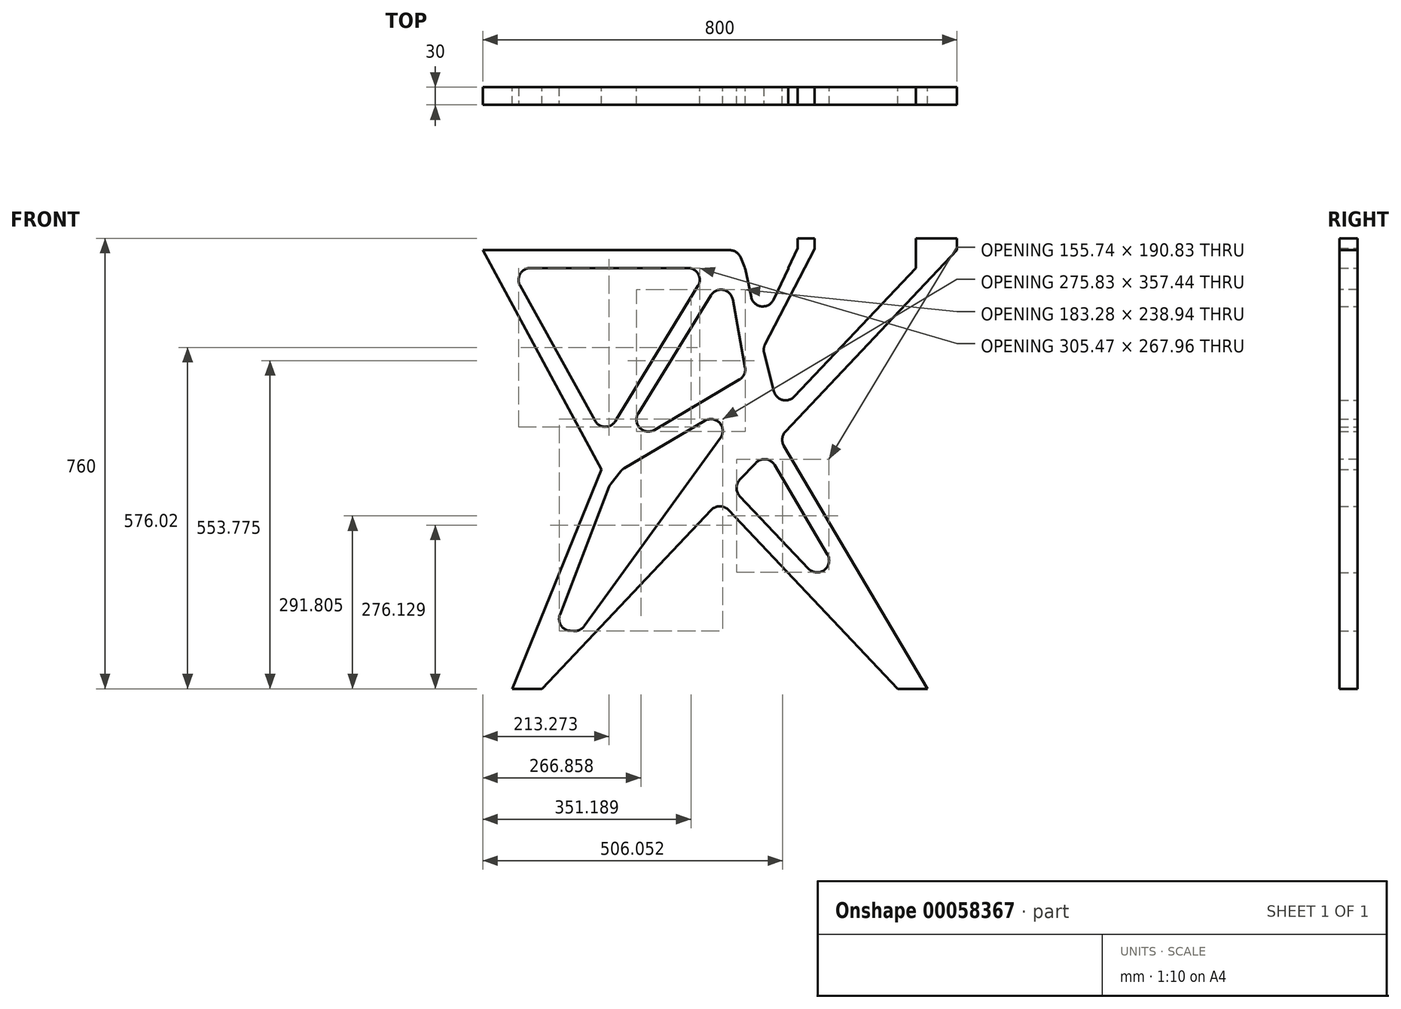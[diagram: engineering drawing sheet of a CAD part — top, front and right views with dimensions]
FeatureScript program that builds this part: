
annotation { "Feature Type Name" : "Feature", "Feature Type Description" : "" }
export const myFeature = defineFeature(function(context is Context, id is Id, definition is map)
    precondition{}
    {
        {
            var Q0;
            Q0=qCreatedBy(makeId("Front.planeOp"),FACE);
            var sketch = newSketch(context, id + "F0", { "sketchPlane" : qUnion([Q0])});
            skLineSegment(sketch, "E0", {"start": v(-40.37, 370) * mm, "end": v(-40.37, -370) * mm, "construction": true});
            skLineSegment(sketch, "E1", {"start": v(-40.37, 370) * mm, "end": v(759.63, 370) * mm, "construction": true});
            skLineSegment(sketch, "E2", {"start": v(-40.37, 370) * mm, "end": v(359.63, 370) * mm, "construction": true});
            skLineSegment(sketch, "E3", {"start": v(-40.37, -370) * mm, "end": v(759.63, -370) * mm, "construction": true});
            skLineSegment(sketch, "E4", {"start": v(759.63, -370) * mm, "end": v(359.63, -370) * mm, "construction": true});
            skLineSegment(sketch, "E5", {"start": v(-40.37, -370) * mm, "end": v(-40.37, 0) * mm, "construction": true});
            skLineSegment(sketch, "E6", {"start": v(-40.37, -370) * mm, "end": v(359.63, -370) * mm, "construction": true});
            skLineSegment(sketch, "E7", {"start": v(159.63, -370) * mm, "end": v(-40.37, -370) * mm, "construction": true});
            skLineSegment(sketch, "E8", {"start": v(59.63, -370) * mm, "end": v(759.63, 370) * mm, "construction": true});
            skLineSegment(sketch, "E9", {"start": v(59.63, -370) * mm, "end": v(-40.37, -370) * mm, "construction": true});
            skLineSegment(sketch, "E10", {"start": v(159.63, 0) * mm, "end": v(9.63, -370) * mm, "construction": true});
            skLineSegment(sketch, "E11", {"start": v(9.63, -370) * mm, "end": v(59.63, -370) * mm});
            skLineSegment(sketch, "E12", {"start": v(759.63, 370) * mm, "end": v(59.63, -370) * mm});
            skLineSegment(sketch, "E13", {"start": v(9.63, -370) * mm, "end": v(159.63, 0) * mm});
            skLineSegment(sketch, "E14", {"start": v(-40.37, 370) * mm, "end": v(159.63, 0) * mm});
            skLineSegment(sketch, "E15", {"start": v(-40.37, 370) * mm, "end": v(-10.37, 370) * mm, "construction": true});
            skLineSegment(sketch, "E16", {"start": v(-10.37, 370) * mm, "end": v(165.48, 52.28) * mm, "construction": true});
            skLineSegment(sketch, "E17", {"start": v(-10.37, 370) * mm, "end": v(359.63, 370) * mm, "construction": true});
            skLineSegment(sketch, "E18", {"start": v(165.48, 52.28) * mm, "end": v(359.63, 370) * mm, "construction": true});
            skLineSegment(sketch, "E19", {"start": v(359.63, 370) * mm, "end": v(389.63, 370) * mm, "construction": true});
            skLineSegment(sketch, "E20", {"start": v(165.48, 52.28) * mm, "end": v(179.74, 25.89) * mm, "construction": true});
            skLineSegment(sketch, "E21", {"start": v(389.63, 370) * mm, "end": v(179.74, 25.89) * mm, "construction": true});
            skLineSegment(sketch, "E22", {"start": v(-40.37, -370) * mm, "end": v(-40.37, -270) * mm, "construction": true});
            skLineSegment(sketch, "E23", {"start": v(154.23, -270) * mm, "end": v(124.23, -273.43) * mm, "construction": true});
            skLineSegment(sketch, "E24", {"start": v(50.17, -270) * mm, "end": v(80.17, -282.16) * mm, "construction": true});
            skLineSegment(sketch, "E25", {"start": v(80.17, -270) * mm, "end": v(173.9, -26.4) * mm, "construction": true});
            skLineSegment(sketch, "E26", {"start": v(173.9, 370) * mm, "end": v(173.9, 340) * mm, "construction": true});
            skLineSegment(sketch, "E27", {"start": v(173.9, 340) * mm, "end": v(6.24, 340) * mm, "construction": true});
            skLineSegment(sketch, "E28", {"start": v(6.24, 340) * mm, "end": v(173.9, 340) * mm, "construction": true});
            skLineSegment(sketch, "E29", {"start": v(173.9, 340) * mm, "end": v(341.3, 340) * mm, "construction": true});
            skLineSegment(sketch, "E30", {"start": v(341.3, 340) * mm, "end": v(389.63, 370) * mm, "construction": true});
            skLineSegment(sketch, "E31", {"start": v(389.63, 370) * mm, "end": v(489.63, 370) * mm, "construction": true});
            skLineSegment(sketch, "E32", {"start": v(416.87, 131.07) * mm, "end": v(194.9, 0) * mm, "construction": true});
            skLineSegment(sketch, "E33", {"start": v(194.9, 0) * mm, "end": v(179.74, 25.89) * mm, "construction": true});
            skLineSegment(sketch, "E34", {"start": v(179.74, 25.89) * mm, "end": v(404.64, 158.69) * mm, "construction": true});
            skLineSegment(sketch, "E35", {"start": v(404.64, 158.69) * mm, "end": v(371.34, 340) * mm, "construction": true});
            skLineSegment(sketch, "E36", {"start": v(371.34, 340) * mm, "end": v(731.26, 340) * mm, "construction": true});
            skLineSegment(sketch, "E37", {"start": v(690.24, 340) * mm, "end": v(401.89, 340) * mm, "construction": true});
            skLineSegment(sketch, "E38", {"start": v(401.89, 340) * mm, "end": v(371.93, 338.33) * mm, "construction": true});
            skLineSegment(sketch, "E39", {"start": v(401.89, 340) * mm, "end": v(459.98, 96.59) * mm, "construction": true});
            skLineSegment(sketch, "E40", {"start": v(389.63, 370) * mm, "end": v(-40.37, 370) * mm});
            skLineSegment(sketch, "E41", {"start": v(359.63, 370) * mm, "end": v(389.63, 370) * mm});
            skLineSegment(sketch, "E42", {"start": v(690.24, 340) * mm, "end": v(459.98, 96.59) * mm});
            skLineSegment(sketch, "E43", {"start": v(690.24, 340) * mm, "end": v(690.24, 370) * mm});
            skLineSegment(sketch, "E44", {"start": v(6.24, 340) * mm, "end": v(341.3, 340) * mm});
            skLineSegment(sketch, "E45", {"start": v(165.48, 52.28) * mm, "end": v(341.3, 340) * mm});
            skLineSegment(sketch, "E46", {"start": v(165.48, 52.28) * mm, "end": v(6.24, 340) * mm});
            skLineSegment(sketch, "E47", {"start": v(371.93, 338.33) * mm, "end": v(404.64, 158.69) * mm});
            skLineSegment(sketch, "E48", {"start": v(179.74, 25.89) * mm, "end": v(371.93, 338.33) * mm});
            skLineSegment(sketch, "E49", {"start": v(401.89, 340) * mm, "end": v(690.24, 340) * mm});
            skLineSegment(sketch, "E50", {"start": v(179.74, 25.89) * mm, "end": v(404.64, 158.69) * mm});
            skLineSegment(sketch, "E51", {"start": v(489.63, 370) * mm, "end": v(424.8, 233.3) * mm, "construction": true});
            skLineSegment(sketch, "E52", {"start": v(490.63, 373.24) * mm, "end": v(519.58, 371.85) * mm, "construction": true});
            skLineSegment(sketch, "E53", {"start": v(424.8, 233.3) * mm, "end": v(432.28, 204.24) * mm, "construction": true});
            skLineSegment(sketch, "E54", {"start": v(690.24, 370) * mm, "end": v(759.63, 370) * mm});
            skLineSegment(sketch, "E55", {"start": v(519.58, 371.85) * mm, "end": v(490.63, 373.24) * mm});
            skLineSegment(sketch, "E56", {"start": v(389.63, 370) * mm, "end": v(359.63, 370) * mm});
            skLineSegment(sketch, "E57", {"start": v(341.3, 340) * mm, "end": v(6.24, 340) * mm});
            skLineSegment(sketch, "E58", {"start": v(-10.37, 370) * mm, "end": v(-40.37, 370) * mm});
            skLineSegment(sketch, "E59", {"start": v(490.63, 373.24) * mm, "end": v(519.58, 371.85) * mm});
            skLineSegment(sketch, "E60", {"start": v(416.87, 131.07) * mm, "end": v(124.23, -273.43) * mm, "construction": true});
            skLineSegment(sketch, "E61", {"start": v(194.9, 0) * mm, "end": v(173.9, -26.4) * mm});
            skLineSegment(sketch, "E62", {"start": v(173.9, -26.4) * mm, "end": v(80.17, -270) * mm});
            skLineSegment(sketch, "E63", {"start": v(80.17, -270) * mm, "end": v(124.23, -273.43) * mm});
            skLineSegment(sketch, "E64", {"start": v(416.87, 131.07) * mm, "end": v(124.23, -273.43) * mm});
            skLineSegment(sketch, "E65", {"start": v(416.87, 131.07) * mm, "end": v(194.9, 0) * mm});
            skLineSegment(sketch, "E66", {"start": v(424.8, 233.3) * mm, "end": v(489.63, 370) * mm});
            skLineSegment(sketch, "E67", {"start": v(519.58, 371.85) * mm, "end": v(432.28, 204.24) * mm});
            skLineSegment(sketch, "E68", {"start": v(389.63, 370) * mm, "end": v(401.89, 340) * mm});
            skLineSegment(sketch, "E69", {"start": v(424.8, 233.3) * mm, "end": v(401.89, 340) * mm});
            skLineSegment(sketch, "E70", {"start": v(432.28, 204.24) * mm, "end": v(459.98, 96.59) * mm});
            skLineSegment(sketch, "E71", {"start": v(-40.37, 370) * mm, "end": v(-40.37, 390) * mm});
            skLineSegment(sketch, "E72", {"start": v(-40.37, 390) * mm, "end": v(-10.37, 390) * mm});
            skLineSegment(sketch, "E73", {"start": v(-10.37, 390) * mm, "end": v(-10.37, 370) * mm});
            skLineSegment(sketch, "E74", {"start": v(359.63, 370) * mm, "end": v(359.63, 390) * mm});
            skLineSegment(sketch, "E75", {"start": v(359.63, 390) * mm, "end": v(389.63, 390) * mm});
            skLineSegment(sketch, "E76", {"start": v(389.63, 390) * mm, "end": v(389.63, 370) * mm});
            skLineSegment(sketch, "E77", {"start": v(490.63, 373.24) * mm, "end": v(490.63, 390) * mm});
            skLineSegment(sketch, "E78", {"start": v(490.63, 390) * mm, "end": v(519.58, 390) * mm});
            skLineSegment(sketch, "E79", {"start": v(519.58, 390) * mm, "end": v(519.58, 371.85) * mm});
            skLineSegment(sketch, "E80", {"start": v(690.24, 370) * mm, "end": v(690.24, 390) * mm});
            skLineSegment(sketch, "E81", {"start": v(690.24, 390) * mm, "end": v(759.63, 390) * mm});
            skLineSegment(sketch, "E82", {"start": v(759.63, 390) * mm, "end": v(759.63, 370) * mm});
            skLineSegment(sketch, "E83", {"start": v(490.63, 373.24) * mm, "end": v(424.8, 233.3) * mm});
            skLineSegment(sketch, "E84", {"start": v(59.63, -370) * mm, "end": v(533.62, 131.07) * mm, "construction": true});
            skLineSegment(sketch, "E85", {"start": v(533.62, 131.07) * mm, "end": v(287.67, -128.93) * mm, "construction": true});
            skLineSegment(sketch, "E86", {"start": v(759.63, -370) * mm, "end": v(709.63, -370) * mm, "construction": true});
            skLineSegment(sketch, "E87", {"start": v(287.67, -128.93) * mm, "end": v(287.67, -370) * mm, "construction": true});
            skLineSegment(sketch, "E88", {"start": v(287.67, -370) * mm, "end": v(515.71, -370) * mm, "construction": true});
            skLineSegment(sketch, "E89", {"start": v(359.63, 390) * mm, "end": v(359.63, -370) * mm, "construction": true});
            skLineSegment(sketch, "E90", {"start": v(359.63, -370) * mm, "end": v(709.63, -370) * mm, "construction": true});
            skLineSegment(sketch, "E91", {"start": v(359.63, -370) * mm, "end": v(659.63, -370) * mm, "construction": true});
            skLineSegment(sketch, "E92", {"start": v(359.63, -52.86) * mm, "end": v(659.63, -370) * mm});
            skLineSegment(sketch, "E93", {"start": v(659.63, -370) * mm, "end": v(709.63, -370) * mm});
            skLineSegment(sketch, "E94", {"start": v(709.63, -370) * mm, "end": v(459.82, 53.06) * mm});
            skLineSegment(sketch, "E95", {"start": v(124.23, -273.43) * mm, "end": v(659.63, -273.43) * mm, "construction": true});
            skLineSegment(sketch, "E96", {"start": v(659.63, -273.43) * mm, "end": v(617.77, -273.43) * mm, "construction": true});
            skLineSegment(sketch, "E97", {"start": v(524.87, -227.54) * mm, "end": v(546.66, -206.92) * mm, "construction": true});
            skLineSegment(sketch, "E98", {"start": v(617.77, -273.43) * mm, "end": v(425.32, 52.5) * mm});
            skLineSegment(sketch, "E99", {"start": v(459.98, 96.59) * mm, "end": v(488.52, 126.75) * mm, "construction": true});
            skLineSegment(sketch, "E100", {"start": v(488.52, 126.75) * mm, "end": v(535.7, 176.63) * mm, "construction": true});
            skLineSegment(sketch, "E101", {"start": v(535.7, 176.63) * mm, "end": v(376.26, 14) * mm, "construction": true});
            skLineSegment(sketch, "E102", {"start": v(425.32, 52.5) * mm, "end": v(419.44, 58.05) * mm});
            skLineSegment(sketch, "E103", {"start": v(546.66, -206.92) * mm, "end": v(617.77, -273.43) * mm});
            skLineSegment(sketch, "E104", {"start": v(546.66, -206.92) * mm, "end": v(359.63, -9.2) * mm});
            skLineSegment(sketch, "E105", {"start": v(359.63, -9.2) * mm, "end": v(359.63, 0) * mm});
            skLineSegment(sketch, "E106", {"start": v(359.63, 0) * mm, "end": v(419.44, 58.05) * mm});
            skLineSegment(sketch, "E107", {"start": v(-40.37, 370) * mm, "end": v(-40.37, 350.76) * mm, "construction": true});
            skLineSegment(sketch, "E108", {"start": v(-40.37, 350.76) * mm, "end": v(519.58, 350.76) * mm, "construction": true});
            skLineSegment(sketch, "E109", {"start": v(519.58, 350.76) * mm, "end": v(759.63, 350.76) * mm, "construction": true});
            skSolve(sketch);
        }
        {
            var Q0;
            Q0=makeQuery(id+"F0.imprint","IMPRINT",FACE,{"disambiguationData":[TD([[makeQuery(id+"F0.imprint","IMPRINT",EDGE,{"derivedFrom":sQuery(id+"F0.wireOp",EDGE,"E11")}),1.0]])]});
            var Q1;
            {var subQ0=sQuery(id+"F0.wireOp",EDGE,"E55");Q1=makeQuery(id+"F0.imprint","IMPRINT",FACE,{"disambiguationData":[TD([[makeQuery(id+"F0.imprint","IMPRINT",EDGE,{"derivedFrom":subQ0}),1.0]])]});}
            var Q2;
            Q2=makeQuery(id+"F0.imprint","IMPRINT",FACE,{"disambiguationData":[TD([[makeQuery(id+"F0.imprint","IMPRINT",EDGE,{"derivedFrom":sQuery(id+"F0.wireOp",EDGE,"E55")}),-1.0]])]});
            var Q3;
            Q3=makeQuery(id+"F0.imprint","IMPRINT",FACE,{"disambiguationData":[TD([[makeQuery(id+"F0.imprint","IMPRINT",EDGE,{"derivedFrom":sQuery(id+"F0.wireOp",EDGE,"E41")}),1.0]])]});
            var Q4;
            Q4=makeQuery(id+"F0.imprint","IMPRINT",FACE,{"disambiguationData":[TD([[makeQuery(id+"F0.imprint","IMPRINT",EDGE,{"derivedFrom":sQuery(id+"F0.wireOp",EDGE,"E54")}),1.0]])]});
            var Q5;
            Q5=makeQuery(id+"F0.imprint","IMPRINT",FACE,{"disambiguationData":[TD([[makeQuery(id+"F0.imprint","IMPRINT",EDGE,{"derivedFrom":sQuery(id+"F0.wireOp",EDGE,"E58")}),-1.0]])]});
            var Q6;
            {var subQ0=sQuery(id+"F0.wireOp",EDGE,"E92");Q6=makeQuery(id+"F0.imprint","IMPRINT",FACE,{"disambiguationData":[TD([[makeQuery(id+"F0.imprint","IMPRINT",EDGE,{"derivedFrom":subQ0}),1.0]])]});}
            var Q7;
            {var subQ4=sQuery(id+"F0.wireOp",EDGE,"E102");Q7=makeQuery(id+"F0.imprint","IMPRINT",FACE,{"disambiguationData":[TD([[makeQuery(id+"F0.imprint","IMPRINT",EDGE,{"derivedFrom":subQ4}),1.0]])]});}
            extrude(context, id + "F1", {"entities" : qUnion([Q0, Q1, Q2, Q3, Q4, Q5, Q6, Q7]), "depth" : 30 * mm});
        }
        {
            var Q0;
            Q0=makeQuery(id+"F1.opExtrude","SWEPT_EDGE",EDGE,{"disambiguationData":[OSD([sQuery(id+"F0.wireOp",EDGE,"E61"),sQuery(id+"F0.wireOp",EDGE,"E62")])]});
            var Q1;
            Q1=makeQuery(id+"F1.opExtrude","SWEPT_EDGE",EDGE,{"disambiguationData":[OSD([sQuery(id+"F0.wireOp",EDGE,"E61"),sQuery(id+"F0.wireOp",EDGE,"E65")])]});
            var Q2;
            Q2=makeQuery(id+"F1.opExtrude","SWEPT_EDGE",EDGE,{"disambiguationData":[OSD([sQuery(id+"F0.wireOp",EDGE,"E64"),sQuery(id+"F0.wireOp",EDGE,"E65")])]});
            var Q3;
            Q3=makeQuery(id+"F1.opExtrude","SWEPT_EDGE",EDGE,{"disambiguationData":[OSD([sQuery(id+"F0.wireOp",EDGE,"E63"),sQuery(id+"F0.wireOp",EDGE,"E64")])]});
            var Q4;
            Q4=makeQuery(id+"F1.opExtrude","SWEPT_EDGE",EDGE,{"disambiguationData":[OSD([sQuery(id+"F0.wireOp",EDGE,"E62"),sQuery(id+"F0.wireOp",EDGE,"E63")])]});
            var Q5;
            Q5=makeQuery(id+"F1.opExtrude","SWEPT_EDGE",EDGE,{"disambiguationData":[OSD([sQuery(id+"F0.wireOp",EDGE,"E48"),sQuery(id+"F0.wireOp",EDGE,"E50")])]});
            var Q6;
            Q6=makeQuery(id+"F1.opExtrude","SWEPT_EDGE",EDGE,{"disambiguationData":[OSD([sQuery(id+"F0.wireOp",EDGE,"E70"),sQuery(id+"F0.wireOp",EDGE,"E67")])]});
            var Q7;
            Q7=makeQuery(id+"F1.opExtrude","SWEPT_EDGE",EDGE,{"disambiguationData":[OSD([sQuery(id+"F0.wireOp",EDGE,"E42"),sQuery(id+"F0.wireOp",EDGE,"E70")])]});
            var Q8;
            Q8=makeQuery(id+"F1.opExtrude","SWEPT_EDGE",EDGE,{"disambiguationData":[OSD([sQuery(id+"F0.wireOp",EDGE,"E66"),sQuery(id+"F0.wireOp",EDGE,"E69"),sQuery(id+"F0.wireOp",EDGE,"E83")])]});
            var Q9;
            Q9=makeQuery(id+"F1.opExtrude","SWEPT_EDGE",EDGE,{"disambiguationData":[OSD([sQuery(id+"F0.wireOp",EDGE,"E47"),sQuery(id+"F0.wireOp",EDGE,"E48")])]});
            var Q10;
            Q10=makeQuery(id+"F1.opExtrude","SWEPT_EDGE",EDGE,{"disambiguationData":[OSD([sQuery(id+"F0.wireOp",EDGE,"E45"),sQuery(id+"F0.wireOp",EDGE,"E46")])]});
            var Q11;
            Q11=makeQuery(id+"F1.opExtrude","SWEPT_EDGE",EDGE,{"disambiguationData":[OSD([sQuery(id+"F0.wireOp",EDGE,"E46"),sQuery(id+"F0.wireOp",EDGE,"E57")])]});
            var Q12;
            Q12=makeQuery(id+"F1.opExtrude","SWEPT_EDGE",EDGE,{"disambiguationData":[OSD([sQuery(id+"F0.wireOp",EDGE,"E45"),sQuery(id+"F0.wireOp",EDGE,"E57")])]});
            var Q13;
            Q13=makeQuery(id+"F1.opExtrude","SWEPT_EDGE",EDGE,{"disambiguationData":[OSD([sQuery(id+"F0.wireOp",EDGE,"E47"),sQuery(id+"F0.wireOp",EDGE,"E50")])]});
            var Q14;
            Q14=makeQuery(id+"F1.opExtrude","SWEPT_EDGE",EDGE,{"disambiguationData":[OSD([sQuery(id+"F0.wireOp",EDGE,"E98"),sQuery(id+"F0.wireOp",EDGE,"E103")])]});
            var Q15;
            Q15=makeQuery(id+"F1.opExtrude","SWEPT_EDGE",EDGE,{"disambiguationData":[OSD([sQuery(id+"F0.wireOp",EDGE,"E12"),sQuery(id+"F0.wireOp",EDGE,"E98")])]});
            var Q16;
            Q16=makeQuery(id+"F1.opExtrude","SWEPT_EDGE",EDGE,{"disambiguationData":[OSD([sQuery(id+"F0.wireOp",EDGE,"E12"),sQuery(id+"F0.wireOp",EDGE,"E104")])]});
            var Q17;
            Q17=makeQuery(id+"F1.opExtrude","SWEPT_EDGE",EDGE,{"disambiguationData":[OSD([sQuery(id+"F0.wireOp",EDGE,"E12"),sQuery(id+"F0.wireOp",EDGE,"E92")])]});
            var Q18;
            Q18=makeQuery(id+"F1.opExtrude","SWEPT_EDGE",EDGE,{"disambiguationData":[OSD([sQuery(id+"F0.wireOp",EDGE,"E12"),sQuery(id+"F0.wireOp",EDGE,"E94")])]});
            var Q19;
            Q19=makeQuery(id+"F1.opExtrude","SWEPT_EDGE",EDGE,{"disambiguationData":[OSD([sQuery(id+"F0.wireOp",EDGE,"E49"),sQuery(id+"F0.wireOp",EDGE,"E68"),sQuery(id+"F0.wireOp",EDGE,"E69")])]});
            var Q20;
            Q20=makeQuery(id+"F1.opExtrude","SWEPT_EDGE",EDGE,{"disambiguationData":[OSD([sQuery(id+"F0.wireOp",EDGE,"E41"),sQuery(id+"F0.wireOp",EDGE,"E68"),sQuery(id+"F0.wireOp",EDGE,"E76")])]});
            fillet(context, id + "F2", {"entities" : qUnion([Q0, Q1, Q2, Q3, Q4, Q5, Q6, Q7, Q8, Q9, Q10, Q11, Q12, Q13, Q14, Q15, Q16, Q17, Q18, Q19, Q20]), "radius" : 20 * mm, "tangentPropagation" : true, "allowEdgeOverflow" : false});
        }
    });
